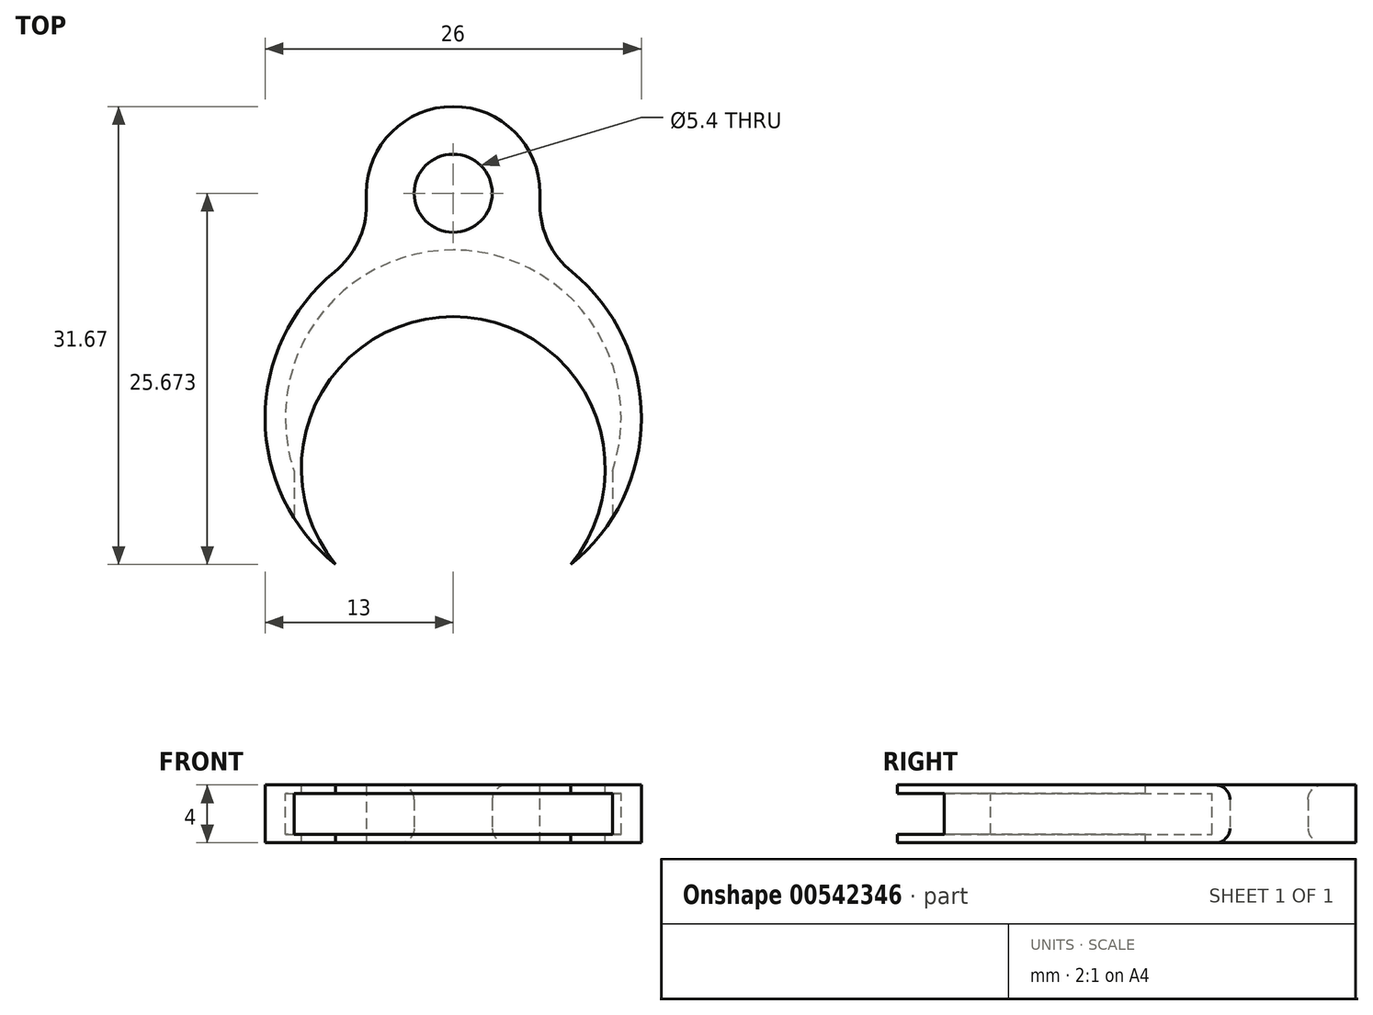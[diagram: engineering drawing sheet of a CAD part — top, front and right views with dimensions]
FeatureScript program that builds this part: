
annotation { "Feature Type Name" : "Feature", "Feature Type Description" : "" }
export const myFeature = defineFeature(function(context is Context, id is Id, definition is map)
    precondition{}
    {
        {
            var Q0;
            Q0=qCreatedBy(makeId("Top.planeOp"),FACE);
            var sketch = newSketch(context, id + "F0", { "sketchPlane" : qUnion([Q0])});
            skCircle(sketch, "E0", {"center": v(0, 0) * mm, "radius": 13 * mm});
            skLineSegment(sketch, "E1.bottom", {"start": v(-6, 11.53) * mm, "end": v(6, 11.53) * mm});
            skLineSegment(sketch, "E1.top", {"start": v(-6, 21.53) * mm, "end": v(6, 21.53) * mm});
            skLineSegment(sketch, "E1.left", {"start": v(-6, 11.53) * mm, "end": v(-6, 21.53) * mm});
            skLineSegment(sketch, "E1.right", {"start": v(6, 11.53) * mm, "end": v(6, 21.53) * mm});
            skCircle(sketch, "E2", {"center": v(0, 15.53) * mm, "radius": 2.7 * mm});
            skPoint(sketch, "E2.centerSnap0", {"position": v(0, 21.53) * mm});
            skSolve(sketch);
        }
        {
            var Q0;
            Q0 = qSketchRegion(id + "F0", true);
            extrude(context, id + "F1", {"entities" : qUnion([Q0]), "endBound" : BoundingType.SYMMETRIC, "depth" : 4 * mm, "offsetDistance" : 25 * mm});
        }
        {
            var Q0;
            Q0=makeQuery(id+"F1.opExtrude","SWEPT_EDGE",EDGE,{"disambiguationData":[OSD([sQuery(id+"F0.wireOp",EDGE,"E1.top"),sQuery(id+"F0.wireOp",EDGE,"E1.left")])]});
            var Q1;
            Q1=makeQuery(id+"F1.opExtrude","SWEPT_EDGE",EDGE,{"disambiguationData":[OSD([sQuery(id+"F0.wireOp",EDGE,"E1.top"),sQuery(id+"F0.wireOp",EDGE,"E1.right")])]});
            var Q2;
            Q2=makeQuery(id+"F1.opExtrude","SWEPT_EDGE",EDGE,{"disambiguationData":[OSD([sQuery(id+"F0.wireOp",EDGE,"E0"),sQuery(id+"F0.wireOp",EDGE,"E1.bottom"),sQuery(id+"F0.wireOp",EDGE,"E1.right")])]});
            var Q3;
            Q3=makeQuery(id+"F1.opExtrude","SWEPT_EDGE",EDGE,{"disambiguationData":[OSD([sQuery(id+"F0.wireOp",EDGE,"E0"),sQuery(id+"F0.wireOp",EDGE,"E1.bottom"),sQuery(id+"F0.wireOp",EDGE,"E1.left")])]});
            fillet(context, id + "F2", {"entities" : qUnion([Q0, Q1, Q2, Q3]), "radius" : 6 * mm, "tangentPropagation" : true, "allowEdgeOverflow" : false});
        }
        {
            var Q0;
            Q0=makeQuery(id+"F1.opExtrude","CAP_EDGE",EDGE,{"disambiguationData":[OSD([sQuery(id+"F0.wireOp",EDGE,"E2")])],"isStart":false});
            var Q1;
            Q1=makeQuery(id+"F1.opExtrude","CAP_EDGE",EDGE,{"disambiguationData":[OSD([sQuery(id+"F0.wireOp",EDGE,"E2")])],"isStart":true});
            fillet(context, id + "F3", {"entities" : qUnion([Q0, Q1]), "radius" : 1 * mm, "tangentPropagation" : true, "allowEdgeOverflow" : false});
        }
        {
            var Q0;
            Q0=makeQuery(id+"F1.opExtrude","CAP_FACE",FACE,{"disambiguationData":[OSD([sQuery(id+"F0.wireOp",EDGE,"E0"),sQuery(id+"F0.wireOp",EDGE,"E1.top"),sQuery(id+"F0.wireOp",EDGE,"E1.left"),sQuery(id+"F0.wireOp",EDGE,"E1.right"),sQuery(id+"F0.wireOp",EDGE,"E2")])],"isStart":false});
            var sketch = newSketch(context, id + "F4", { "sketchPlane" : qUnion([Q0])});
            skCircle(sketch, "E3", {"center": v(0, -3.5) * mm, "radius": 10.5 * mm});
            skSolve(sketch);
        }
        {
            var Q0;
            Q0 = qSketchRegion(id + "F4", true);
            extrude(context, id + "F5", {"entities" : qUnion([Q0]), "operationType" : NewBodyOperationType.REMOVE, "endBound" : BoundingType.THROUGH_ALL, "oppositeDirection" : true, "depth" : 25 * mm, "offsetDistance" : 25 * mm});
        }
        {
            var Q0;
            Q0=qCreatedBy(makeId("Top.planeOp"),FACE);
            var sketch = newSketch(context, id + "F6", { "sketchPlane" : qUnion([Q0])});
            skCircle(sketch, "E4", {"center": v(0, 0) * mm, "radius": 11.6 * mm});
            skLineSegment(sketch, "E5.bottom", {"start": v(-11, -3.7) * mm, "end": v(11, -3.7) * mm});
            skLineSegment(sketch, "E5.top", {"start": v(-11, -14.15) * mm, "end": v(11, -14.15) * mm});
            skLineSegment(sketch, "E5.left", {"start": v(-11, -3.7) * mm, "end": v(-11, -14.15) * mm});
            skLineSegment(sketch, "E5.right", {"start": v(11, -3.7) * mm, "end": v(11, -14.15) * mm});
            skSolve(sketch);
        }
        {
            var Q0;
            Q0 = qSketchRegion(id + "F6", true);
            extrude(context, id + "F7", {"entities" : qUnion([Q0]), "operationType" : NewBodyOperationType.REMOVE, "endBound" : BoundingType.SYMMETRIC, "oppositeDirection" : true, "depth" : 2.8 * mm, "offsetDistance" : 25 * mm});
        }
    });
